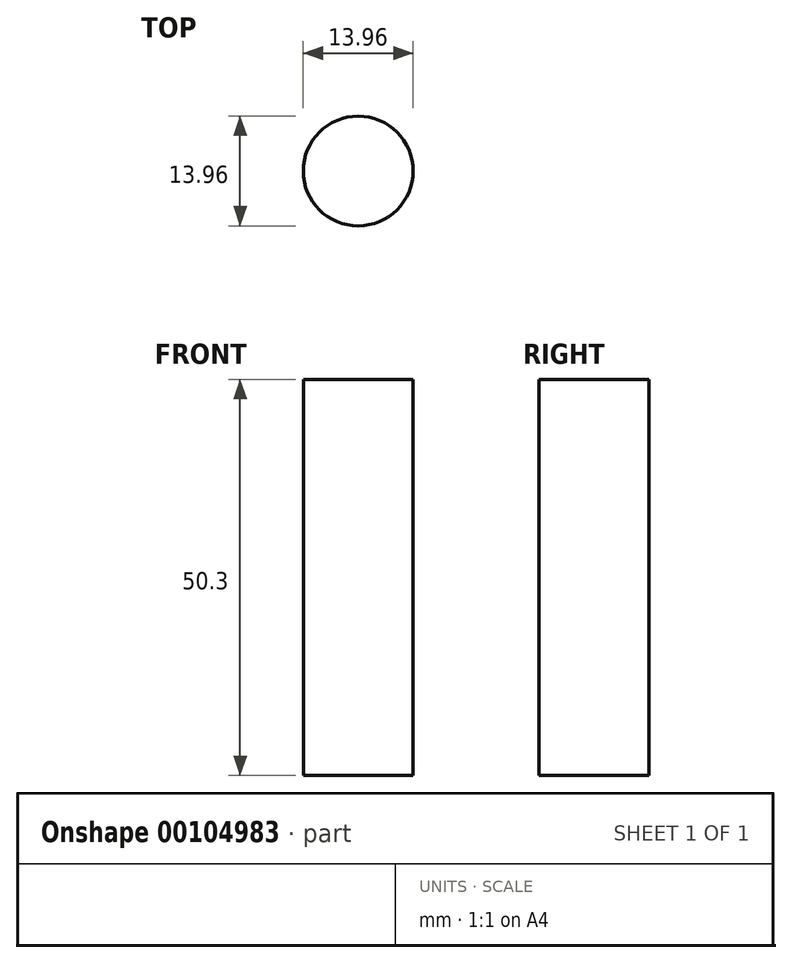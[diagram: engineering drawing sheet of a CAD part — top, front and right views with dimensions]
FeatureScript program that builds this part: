
annotation { "Feature Type Name" : "Feature", "Feature Type Description" : "" }
export const myFeature = defineFeature(function(context is Context, id is Id, definition is map)
    precondition{}
    {
        {
            var Q0;
            Q0=qCreatedBy(makeId("Top.planeOp"),FACE);
            var sketch = newSketch(context, id + "F0", { "sketchPlane" : qUnion([Q0])});
            skCircle(sketch, "E0", {"center": v(0, 0) * mm, "radius": 6.98 * mm});
            skSolve(sketch);
        }
        {
            var Q0;
            Q0=makeQuery(id+"F0.imprint","IMPRINT",FACE,{"disambiguationData":[TD([[makeQuery(id+"F0.imprint","IMPRINT",EDGE,{"derivedFrom":sQuery(id+"F0.wireOp",EDGE,"E0")}),1.0]])]});
            extrude(context, id + "F1", {"entities" : qUnion([Q0]), "depth" : 50.3 * mm});
        }
    });
